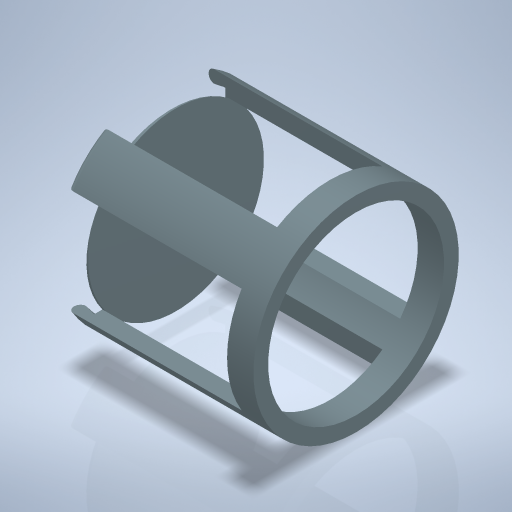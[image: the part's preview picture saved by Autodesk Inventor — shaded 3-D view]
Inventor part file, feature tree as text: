
AUTODESK INVENTOR PART (.ipt)
format: ipt  version: 2024 (Build 280153000, 153)  size: 361,472 bytes
history: native  units: mm
features: sketch x4, extrude x3, plane x2, pattern_circular x2, revolve x1
ambient origin geometry x8: Origin, YZ Plane, XZ Plane, XY Plane, X Axis, Y Axis, Z Axis, Center Point
bodies: Volumenkörper1 (feature_tree)
feature tree (12):
  revolve  "Umdrehung1"
  extrude  "Extrusion2"  Depth=39.0mm
  plane  "Arbeitsebene2"
  extrude  "Extrusion5"  Depth=33.4mm
  pattern_circular  "Runde Anordnung3"  [2 undecoded]
  plane  "Arbeitsebene5"
  extrude  "Extrusion8"  Depth=20.0mm
  pattern_circular  "Runde Anordnung4"  Count=4 Angle=360.0deg
  sketch  "Skizze1"  dims[d0=35.0mm d3=39.0mm]
  sketch  "Skizze4"  dims[d6=360.0deg d18=33.4mm]
  sketch  "Skizze5"  dims[d19=34.2mm d20=0.0mm]
  sketch  "Skizze8"  dims[d21=19.5mm d22=5.0mm d23=20.0mm d27=40.0mm d28=360.0deg d31=36.0mm d32=0.2mm d33=38.0mm d35=1.0mm d38=1.5mm d39=10.0mm d40=0.0mm d47=19.5mm d49=10.0mm d50=0.0mm d51=40.0mm d52=360.0deg d54=34.8mm]
note: 2 required parameter values undecoded (feature->parameter linkage not recoverable at this tier; creation-order binding heuristic only, values carry confidence <= 0.55)
